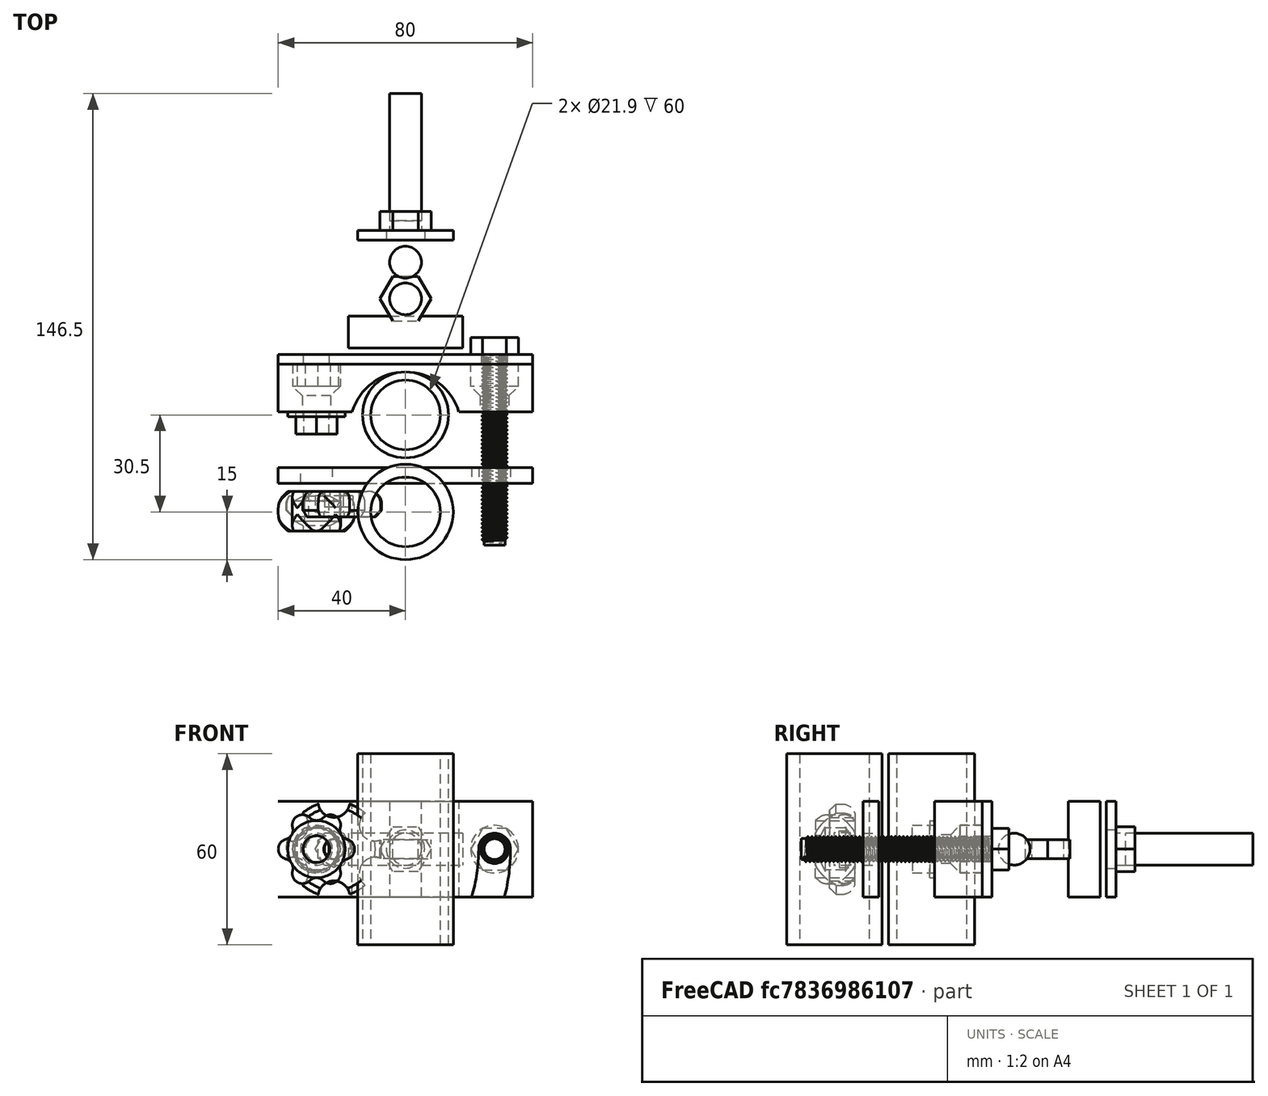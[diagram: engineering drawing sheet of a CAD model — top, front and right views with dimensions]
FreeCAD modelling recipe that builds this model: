
FCSTD DOCUMENT  (FreeCAD 1.0R39109 (Git))
Label: attache_remorque_V2
License: All rights reserved
LicenseURL: http://en.wikipedia.org/wiki/All_rights_reserved
objects: Sketcher::SketchObject×26, TechDraw::DrawViewBalloon×24, PartDesign::Body×16, PartDesign::Pad×15, TechDraw::DrawViewDimension×14, Part::FeaturePython×13, PartDesign::Pocket×6, TechDraw::DrawViewPart×4, PartDesign::Revolution×2, PartDesign::Groove×2, TechDraw::DrawSVGTemplate×1, PartDesign::AdditiveHelix×1, Spreadsheet::Sheet×1, TechDraw::DrawViewAnnotation×1, TechDraw::DrawPage×1
note: 159 computed .brp shape members not serialized (recipe doc carries the construction recipe); baked Part::Feature solids carry a one-line shape summary decoded from their .brp

FEATURE [Sketcher::SketchObject] Sketch
  ArcFitTolerance = 0
  AttachmentSupport = -> [XY_Plane]
  FullyConstrained = true
  MakeInternals = false
  MapMode = 5
  sketch-geometry (8):
    g0: LineSegment StartX=7 StartY=4.04145 StartZ=0 EndX=2.7e-15 EndY=8.0829 EndZ=0
    g1: LineSegment StartX=2.7e-15 StartY=8.0829 StartZ=0 EndX=-7 EndY=4.04145 EndZ=0
    g2: LineSegment StartX=-7 StartY=4.04145 StartZ=0 EndX=-7 EndY=-4.04145 EndZ=0
    g3: LineSegment StartX=-7 StartY=-4.04145 StartZ=0 EndX=4.17e-14 EndY=-8.0829 EndZ=0
    g4: LineSegment StartX=4.17e-14 StartY=-8.0829 StartZ=0 EndX=7 EndY=-4.04145 EndZ=0
    g5: LineSegment StartX=7 StartY=-4.04145 StartZ=0 EndX=7 EndY=4.04145 EndZ=0
    g6: Circle [constr] CenterX=0 CenterY=0 CenterZ=0 NormalX=0 NormalY=0 NormalZ=1 AngleXU=0 Radius=8.0829
    g7: Circle CenterX=0 CenterY=0 CenterZ=0 NormalX=0 NormalY=0 NormalZ=1 AngleXU=0 Radius=5
  constraints (18):
    c: Coincident(g0,g1)
    c: Coincident(g1,g2)
    c: Coincident(g2,g3)
    c: Coincident(g3,g4)
    c: Coincident(g4,g5)
    c: Coincident(g5,g0)
    c: Equal(g0, g1-g5) x5
    c: PointOnObject(g0,g6)
    c: PointOnObject(g1,g6)
    c: PointOnObject(g2,g6)
    c: PointOnObject(g3,g6)
    c: PointOnObject(g4,g6)
    c: PointOnObject(g5,g6)
    c: Coincident(g6,g-1)
    c: Vertical(g5)
    c: DistanceX(g2,g4) = 14
    c: Coincident(g7,g6)
    c: Radius(g7) = 5
FEATURE [PartDesign::Pad] Pad
  Direction = (0,0,1)
  Length = 6
  Length2 = 10
  Profile = -> Sketch
  ReferenceAxis = -> Sketch [N_Axis]
  Suppressed = false
  Type = 0
FEATURE [PartDesign::Body] Body  label="Ecrou M10"
  AllowCompound = false
  Group = -> [Sketch,Pad]
  Origin = -> Origin
  Placement = pos=(4e-16,2,-15) rot=(0,0,-1;0.523599rad)
  Tip = -> Pad
  expr: .Placement.Base.y = 2 + Spreadsheet.eclate * 80
  expr: .Placement.Base.z = -15 - Spreadsheet.eclate * 10
FEATURE [Sketcher::SketchObject] Sketch001
  ArcFitTolerance = 0
  AttachmentSupport = -> [XY_Plane001]
  FullyConstrained = true
  MakeInternals = false
  MapMode = 5
  sketch-geometry (1):
    g0: Circle CenterX=0 CenterY=0 CenterZ=0 NormalX=0 NormalY=0 NormalZ=1 AngleXU=0 Radius=5
  constraints (2):
    c: Coincident(g0,g-1)
    c: Radius(g0) = 5
FEATURE [PartDesign::Pad] Pad001
  Direction = (0,0,1)
  Length = 30
  Length2 = 10
  Midplane = true
  Profile = -> Sketch001
  ReferenceAxis = -> Sketch001 [N_Axis]
  Suppressed = false
  Type = 0
FEATURE [PartDesign::Body] Body001  label="Tige Filetée M10x30"
  AllowCompound = false
  Group = -> [Sketch001,Pad001]
  Origin = -> Origin001
  Placement = pos=(0,2,0) rot=(0,0,1;0rad)
  Tip = -> Pad001
  expr: .Placement.Base.y = 2 + Spreadsheet.eclate * 80
FEATURE [Part::FeaturePython] Clone  label="Ecrou M011"  # Draft clone (typed FeaturePython)
  AttacherType = Attacher::AttachEngine3D
  Fuse = false
  Objects = -> [Body]
  Placement = pos=(1.3e-15,2,9) rot=(0,0,-1;0.523599rad)
  Scale = (1,1,1)
  expr: .Placement.Base.y = 2 + Spreadsheet.eclate * 80
  expr: .Placement.Base.z = 9 + Spreadsheet.eclate * 10
FEATURE [Sketcher::SketchObject] Sketch002
  ArcFitTolerance = 0
  AttachmentSupport = -> [XY_Plane002]
  FullyConstrained = true
  MakeInternals = false
  MapMode = 5
  sketch-geometry (1):
    g0: Circle CenterX=0 CenterY=0 CenterZ=0 NormalX=0 NormalY=0 NormalZ=1 AngleXU=0 Radius=5
  constraints (2):
    c: Coincident(g0,g-1)
    c: Radius(g0) = 5
FEATURE [PartDesign::Pad] Pad002
  Direction = (0,0,1)
  Length = 36
  Length2 = 10
  Midplane = true
  Profile = -> Sketch002
  ReferenceAxis = -> Sketch002 [N_Axis]
  Suppressed = false
  Type = 0
FEATURE [PartDesign::Body] Body002  label="Tige Filetée M10 x 36"
  AllowCompound = false
  Group = -> [Sketch002,Pad002]
  Origin = -> Origin002
  Placement = pos=(0,-20,0) rot=(0,-1,0;1.5708rad)
  Tip = -> Pad002
  expr: .Placement.Base.y = -20 + Spreadsheet.eclate * 60
FEATURE [Part::FeaturePython] Clone001  label="Ecrou M012"  # Draft clone (typed FeaturePython)
  AttacherType = Attacher::AttachEngine3D
  Fuse = false
  Objects = -> [Clone]
  Placement = pos=(12,-20,0) rot=(-0.248932,0.935984,-0.248932;1.63782rad)
  Scale = (1,1,1)
  expr: .Placement.Base.x = 12 + Spreadsheet.eclate * 10
  expr: .Placement.Base.y = -20 + Spreadsheet.eclate * 60
FEATURE [Part::FeaturePython] Clone002  label="Ecrou M013"  # Draft clone (typed FeaturePython)
  AttacherType = Attacher::AttachEngine3D
  Fuse = false
  Objects = -> [Clone001]
  Placement = pos=(-18,-20,0) rot=(0.57735,0.57735,0.57735;2.0944rad)
  Scale = (1,1,1)
  expr: .Placement.Base.x = -18 - Spreadsheet.eclate * 10
  expr: .Placement.Base.y = -20 + Spreadsheet.eclate * 60
FEATURE [Sketcher::SketchObject] Sketch003
  ArcFitTolerance = 0
  AttachmentSupport = -> [YZ_Plane003]
  FullyConstrained = true
  MakeInternals = false
  MapMode = 5
  Placement = pos=(0,0,0) rot=(0.57735,0.57735,0.57735;2.0944rad)
  sketch-geometry (4):
    g0: LineSegment StartX=0 StartY=15 StartZ=0 EndX=3 EndY=15 EndZ=0
    g1: LineSegment StartX=3 StartY=15 StartZ=0 EndX=3 EndY=-15 EndZ=0
    g2: LineSegment StartX=3 StartY=-15 StartZ=0 EndX=0 EndY=-15 EndZ=0
    g3: LineSegment StartX=0 StartY=-15 StartZ=0 EndX=0 EndY=15 EndZ=0
  constraints (11):
    c: Coincident(g0,g1)
    c: Coincident(g1,g2)
    c: Coincident(g2,g3)
    c: Coincident(g3,g0)
    c: Horizontal(g0)
    c: Horizontal(g2)
    c: Vertical(g3)
    c: PointOnObject(g0,g-2)
    c: DistanceX(g2,g2) = 3
    c: Symmetric(g1,g0,g-1)
    c: DistanceY(g1,g1) = 30
FEATURE [PartDesign::Pad] Pad003
  Direction = (1,0,0)
  Length = 30
  Length2 = 10
  Midplane = true
  Placement = pos=(0,0,0) rot=(0.57735,0.57735,0.57735;2.0944rad)
  Profile = -> Sketch003
  ReferenceAxis = -> Sketch003 [N_Axis]
  Suppressed = false
  Type = 0
FEATURE [Part::FeaturePython] Clone003  label="Ecrou M014"  # Draft clone (typed FeaturePython)
  AttacherType = Attacher::AttachEngine3D
  Fuse = false
  Objects = -> [Clone002]
  Placement = pos=(0,12,0) rot=(-0.57735,0.57735,0.57735;2.0944rad)
  Scale = (1,1,1)
  expr: .Placement.Base.y = 12 + Spreadsheet.eclate * 100
FEATURE [Sketcher::SketchObject] Sketch004
  ArcFitTolerance = 0
  AttachmentSupport = -> [XY_Plane004]
  FullyConstrained = true
  MakeInternals = false
  MapMode = 5
  sketch-geometry (1):
    g0: Circle CenterX=0 CenterY=0 CenterZ=0 NormalX=0 NormalY=0 NormalZ=1 AngleXU=0 Radius=5
  constraints (2):
    c: Coincident(g0,g-1)
    c: Radius(g0) = 5
FEATURE [PartDesign::Pad] Pad004
  Direction = (0,0,1)
  Length = 40
  Length2 = 10
  Midplane = true
  Profile = -> Sketch004
  ReferenceAxis = -> Sketch004 [N_Axis]
  Suppressed = false
  Type = 0
FEATURE [PartDesign::Body] Body004  label="Tige Filetée M10 002"
  AllowCompound = false
  Group = -> [Sketch004,Pad004]
  Origin = -> Origin004
  Placement = pos=(0,35,0) rot=(0.57735,-0.57735,-0.57735;4.18879rad)
  Tip = -> Pad004
  expr: .Placement.Base.y = 35 + Spreadsheet.eclate * 110
FEATURE [Sketcher::SketchObject] Sketch005
  ArcFitTolerance = 0
  AttachmentSupport = -> [XY_Plane005]
  FullyConstrained = false
  MakeInternals = false
  MapMode = 5
  sketch-geometry (2):
    g0: Circle CenterX=0 CenterY=-13.5 CenterZ=0 NormalX=0 NormalY=0 NormalZ=1 AngleXU=0 Radius=13.5
    g1: Circle CenterX=0 CenterY=-13.5 CenterZ=0 NormalX=0 NormalY=0 NormalZ=1 AngleXU=0 Radius=10.9492
  constraints (4):
    c: Radius(g0) = 13.5
    c: Coincident(g1,g0)
    c: PointOnObject(g0,g-2)
    c: Tangent(g0,g-1)
FEATURE [PartDesign::Pad] Pad005
  Direction = (0,0,1)
  Length = 60
  Length2 = 10
  Midplane = true
  Profile = -> Sketch005
  ReferenceAxis = -> Sketch005 [N_Axis]
  Suppressed = false
  Type = 0
FEATURE [PartDesign::Body] Body005  label="Tige de selle 27mm"
  AllowCompound = false
  Group = -> [Sketch005,Pad005]
  Origin = -> Origin005
  Placement = pos=(0,-32.5,0) rot=(0,0,1;0rad)
  Tip = -> Pad005
FEATURE [Part::FeaturePython] Clone004  label="Ecrou M015"  # Draft clone (typed FeaturePython)
  AttacherType = Attacher::AttachEngine3D
  Fuse = false
  Objects = -> [Body]
  Placement = pos=(0,-9.5,-3) rot=(0,0,-1;5.75959rad)
  Scale = (1,1,1)
  expr: .Placement.Base.y = -9.5 + Spreadsheet.eclate * 70
FEATURE [Sketcher::SketchObject] Sketch007
  ArcFitTolerance = 0
  AttachmentSupport = -> [XY_Plane007]
  FullyConstrained = true
  MakeInternals = false
  MapMode = 5
  sketch-geometry (6):
    g0: LineSegment StartX=-16.7705 StartY=-15 StartZ=0 EndX=-40 EndY=-15 EndZ=0
    g1: LineSegment StartX=-40 StartY=-15 StartZ=0 EndX=-40 EndY=0 EndZ=0
    g2: LineSegment StartX=-40 StartY=0 StartZ=0 EndX=40 EndY=0 EndZ=0
    g3: LineSegment StartX=40 StartY=0 StartZ=0 EndX=40 EndY=-15 EndZ=0
    g4: LineSegment StartX=40 StartY=-15 StartZ=0 EndX=16.7705 EndY=-15 EndZ=0
    g5: ArcOfCircle CenterX=5e-16 CenterY=-20 CenterZ=0 NormalX=0 NormalY=0 NormalZ=1 AngleXU=0 Radius=17.5 StartAngle=0.289752 EndAngle=2.85184
  constraints (17):
    c: Horizontal(g0)
    c: Coincident(g0,g1)
    c: PointOnObject(g1,g-1)
    c: Vertical(g1)
    c: Coincident(g1,g2)
    c: PointOnObject(g2,g-1)
    c: Coincident(g2,g3)
    c: Vertical(g3)
    c: Coincident(g3,g4)
    c: Coincident(g5,g0)
    c: Coincident(g5,g4)
    c: Radius(g5) = 17.5
    c: Symmetric(g0,g4,g-2)
    c: Symmetric(g3,g0,g-2)
    c: DistanceX(g2,g2) = 80
    c: DistanceY(g3,g3) = 15
    c: DistanceY(g5) = -20
FEATURE [PartDesign::Pad] Pad007
  Direction = (0,0,1)
  Length = 30
  Length2 = 10
  Midplane = true
  Profile = -> Sketch007
  ReferenceAxis = -> Sketch007 [N_Axis]
  Suppressed = false
  Type = 0
FEATURE [Sketcher::SketchObject] Sketch010
  ArcFitTolerance = 0
  AttachmentSupport = -> [XY_Plane008]
  FullyConstrained = true
  MakeInternals = false
  MapMode = 5
  sketch-geometry (5):
    g0: LineSegment StartX=0 StartY=0 StartZ=0 EndX=-40 EndY=0 EndZ=0
    g1: LineSegment StartX=-40 StartY=0 StartZ=0 EndX=-40 EndY=-5 EndZ=0
    g2: LineSegment StartX=-40 StartY=-5 StartZ=0 EndX=40 EndY=-5 EndZ=0
    g3: LineSegment StartX=40 StartY=-5 StartZ=0 EndX=40 EndY=0 EndZ=0
    g4: LineSegment StartX=40 StartY=0 StartZ=0 EndX=0 EndY=0 EndZ=0
  constraints (14):
    c: PointOnObject(g0,g-1)
    c: PointOnObject(g0,g-1)
    c: Coincident(g0,g1)
    c: Vertical(g1)
    c: Coincident(g1,g2)
    c: Coincident(g2,g3)
    c: Vertical(g3)
    c: Coincident(g3,g4)
    c: Horizontal(g4)
    c: Symmetric(g2,g1,g-2)
    c: DistanceY(g3,g3) = 5
    c: DistanceX(g2,g2) = 80
    c: Coincident(g4,g0)
    c: PointOnObject(g0,g-2)
FEATURE [PartDesign::Pad] Pad009
  Direction = (0,0,1)
  Length = 30
  Length2 = 10
  Midplane = true
  Profile = -> Sketch010
  ReferenceAxis = -> Sketch010 [N_Axis]
  Suppressed = false
  Type = 0
FEATURE [Sketcher::SketchObject] Sketch011
  ArcFitTolerance = 0
  AttachmentSupport = -> [XZ_Plane008]
  FullyConstrained = true
  MakeInternals = false
  MapMode = 5
  Placement = pos=(0,0,0) rot=(1,0,0;1.5708rad)
  sketch-geometry (5):
    g0: ArcOfCircle CenterX=-28 CenterY=0 CenterZ=0 NormalX=0 NormalY=0 NormalZ=1 AngleXU=0 Radius=51 StartAngle=5.98465 EndAngle=6.28319
    g1: ArcOfCircle CenterX=-28 CenterY=0 CenterZ=0 NormalX=0 NormalY=0 NormalZ=1 AngleXU=0 Radius=61 StartAngle=6.03474 EndAngle=6.28319
    g2: LineSegment StartX=20.7442 StartY=-15 StartZ=0 EndX=31.127 EndY=-15 EndZ=0
    g3: ArcOfCircle CenterX=28 CenterY=0 CenterZ=0 NormalX=0 NormalY=0 NormalZ=1 AngleXU=0 Radius=5 StartAngle=0 EndAngle=3.14159
    g4: Circle CenterX=-28 CenterY=0 CenterZ=0 NormalX=0 NormalY=0 NormalZ=1 AngleXU=0 Radius=5
  constraints (13):
    c: Coincident(g1,g0)
    c: Coincident(g2,g0)
    c: Coincident(g2,g1)
    c: PointOnObject(g3,g-1)
    c: Radius(g3) = 5
    c: DistanceX(g3) = 28
    c: Horizontal(g2)
    c: Tangent(g3,g0) = 1.5708
    c: Tangent(g3,g1) = -1.5708
    c: DistanceY(g1) = -15
    c: Equal(g4,g3)
    c: Symmetric(g3,g4,g-2)
    c: Coincident(g0,g4)
FEATURE [PartDesign::Pocket] Pocket001
  BaseFeature = -> Pad009
  Direction = (0,1,-2e-16)
  Length = 5
  Length2 = 5
  Profile = -> Sketch011
  ReferenceAxis = -> Sketch011 [N_Axis]
  Reversed = true
  Suppressed = false
  Type = 0
FEATURE [PartDesign::Body] Body008  label="Contre plaque selle"
  AllowCompound = false
  Group = -> [Sketch010,Pad009,Sketch011,Pocket001]
  Origin = -> Origin008
  Placement = pos=(0,-62.5,0) rot=(0,0,1;0rad)
  Tip = -> Pocket001
  expr: .Placement.Base.y = -62.5 - Spreadsheet.eclate * 10
FEATURE [Sketcher::SketchObject] Sketch012
  ArcFitTolerance = 0
  AttachmentSupport = -> [XY_Plane009]
  FullyConstrained = true
  MakeInternals = false
  MapMode = 5
  sketch-geometry (8):
    g0: LineSegment StartX=5 StartY=2.88675 StartZ=0 EndX=9.4058e-12 EndY=5.7735 EndZ=0
    g1: LineSegment StartX=9.4058e-12 StartY=5.7735 StartZ=0 EndX=-5 EndY=2.88675 EndZ=0
    g2: LineSegment StartX=-5 StartY=2.88675 StartZ=0 EndX=-5 EndY=-2.88675 EndZ=0
    g3: LineSegment StartX=-5 StartY=-2.88675 StartZ=0 EndX=-1.4424e-12 EndY=-5.7735 EndZ=0
    g4: LineSegment StartX=-1.4424e-12 StartY=-5.7735 StartZ=0 EndX=5 EndY=-2.88675 EndZ=0
    g5: LineSegment StartX=5 StartY=-2.88675 StartZ=0 EndX=5 EndY=2.88675 EndZ=0
    g6: Circle [constr] CenterX=0 CenterY=0 CenterZ=0 NormalX=0 NormalY=0 NormalZ=1 AngleXU=0 Radius=5.7735
    g7: Circle CenterX=0 CenterY=0 CenterZ=0 NormalX=0 NormalY=0 NormalZ=1 AngleXU=0 Radius=3
  constraints (18):
    c: Coincident(g0,g1)
    c: Coincident(g1,g2)
    c: Coincident(g2,g3)
    c: Coincident(g3,g4)
    c: Coincident(g4,g5)
    c: Coincident(g5,g0)
    c: Equal(g0, g1-g5) x5
    c: PointOnObject(g0,g6)
    c: PointOnObject(g1,g6)
    c: PointOnObject(g2,g6)
    c: PointOnObject(g3,g6)
    c: PointOnObject(g4,g6)
    c: PointOnObject(g5,g6)
    c: Coincident(g6,g-1)
    c: Vertical(g5)
    c: DistanceX(g2,g4) = 10
    c: Coincident(g7,g6)
    c: Radius(g7) = 3
FEATURE [PartDesign::Pad] Pad010
  Direction = (0,0,1)
  Length = 5
  Length2 = 10
  Profile = -> Sketch012
  ReferenceAxis = -> Sketch012 [N_Axis]
  Suppressed = false
  Type = 0
FEATURE [PartDesign::Body] Body009  label="Ecrou M6 001"
  AllowCompound = false
  Group = -> [Sketch012,Pad010]
  Origin = -> Origin009
  Placement = pos=(22.5,-75,-4e-15) rot=(1,0,0;4.71239rad)
  Tip = -> Pad010
FEATURE [Part::FeaturePython] Clone005  label="Ecrou M6 002"  # Draft clone (typed FeaturePython)
  AttacherType = Attacher::AttachEngine3D
  Fuse = false
  Objects = -> [Body009]
  Placement = pos=(-22.5,-75,-4e-15) rot=(1,0,0;4.71239rad)
  Scale = (1,1,1)
FEATURE [Sketcher::SketchObject] Sketch013
  ArcFitTolerance = 0
  AttachmentSupport = -> [XY_Plane010]
  FullyConstrained = false
  MakeInternals = false
  MapMode = 5
  sketch-geometry (2):
    g0: Circle CenterX=0 CenterY=-15 CenterZ=0 NormalX=0 NormalY=0 NormalZ=1 AngleXU=0 Radius=15
    g1: Circle CenterX=0 CenterY=-15 CenterZ=0 NormalX=0 NormalY=0 NormalZ=1 AngleXU=0 Radius=10.9492
  constraints (4):
    c: Radius(g0) = 15
    c: Coincident(g1,g0)
    c: PointOnObject(g0,g-2)
    c: Tangent(g0,g-1)
FEATURE [PartDesign::Pad] Pad011
  Direction = (0,0,1)
  Length = 60
  Length2 = 10
  Midplane = true
  Profile = -> Sketch013
  ReferenceAxis = -> Sketch013 [N_Axis]
  Suppressed = false
  Type = 0
FEATURE [PartDesign::Body] Body010  label="Tige de selle 30mm"
  AllowCompound = false
  Group = -> [Sketch013,Pad011]
  Origin = -> Origin010
  Placement = pos=(0,-61.5,0) rot=(0,0,1;0rad)
  Tip = -> Pad011
FEATURE [Sketcher::SketchObject] Sketch014
  ArcFitTolerance = 0
  AttachmentSupport = -> [XZ_Plane011]
  FullyConstrained = true
  MakeInternals = false
  MapMode = 5
  Placement = pos=(0,0,0) rot=(1,0,0;1.5708rad)
  sketch-geometry (6):
    g0: ArcOfCircle CenterX=11 CenterY=-4 CenterZ=0 NormalX=0 NormalY=0 NormalZ=1 AngleXU=0 Radius=4 StartAngle=0 EndAngle=1.5708
    g1: LineSegment StartX=3.2 StartY=0 StartZ=0 EndX=3.2 EndY=-8 EndZ=0
    g2: LineSegment StartX=3.2 StartY=-8 StartZ=0 EndX=13 EndY=-8 EndZ=0
    g3: LineSegment StartX=15 StartY=-6 StartZ=0 EndX=15 EndY=-4 EndZ=0
    g4: LineSegment StartX=13 StartY=-8 StartZ=0 EndX=15 EndY=-6 EndZ=0
    g5: LineSegment StartX=3.2 StartY=0 StartZ=0 EndX=11 EndY=0 EndZ=0
  constraints (17):
    c: Vertical(g1)
    c: Coincident(g1,g2)
    c: Horizontal(g2)
    c: Vertical(g3)
    c: Tangent(g3,g0) = -1.5708
    c: DistanceX(g1) = 3.2
    c: DistanceX(g3) = 15
    c: DistanceY(g3,g3) = 2
    c: Coincident(g4,g2)
    c: Coincident(g4,g3)
    c: DistanceX(g4,g4) = 2
    c: DistanceY(g4,g4) = 2
    c: Coincident(g1,g5)
    c: PointOnObject(g1,g-1)
    c: Horizontal(g5)
    c: Tangent(g5,g0) = 1.5708
    c: DistanceY(g2,g0) = 8
FEATURE [Sketcher::SketchObject] Sketch015
  ArcFitTolerance = 0
  AttachmentOffset = pos=(0,0,-1.5) rot=(0,0,1;0rad)
  AttachmentSupport = -> [XY_Plane011]
  FullyConstrained = true
  MakeInternals = false
  MapMode = 5
  Placement = pos=(0,0,-1.5) rot=(0,0,1;0rad)
  sketch-geometry (7):
    g0: LineSegment StartX=5.88897 StartY=0 StartZ=0 EndX=2.94449 EndY=5.1 EndZ=0
    g1: LineSegment StartX=2.94449 StartY=5.1 StartZ=0 EndX=-2.94449 EndY=5.1 EndZ=0
    g2: LineSegment StartX=-2.94449 StartY=5.1 StartZ=0 EndX=-5.88897 EndY=0 EndZ=0
    g3: LineSegment StartX=-5.88897 StartY=0 StartZ=0 EndX=-2.94449 EndY=-5.1 EndZ=0
    g4: LineSegment StartX=-2.94449 StartY=-5.1 StartZ=0 EndX=2.94449 EndY=-5.1 EndZ=0
    g5: LineSegment StartX=2.94449 StartY=-5.1 StartZ=0 EndX=5.88897 EndY=0 EndZ=0
    g6: Circle [constr] CenterX=0 CenterY=0 CenterZ=0 NormalX=0 NormalY=0 NormalZ=1 AngleXU=0 Radius=5.88897
  constraints (16):
    c: Coincident(g0,g1)
    c: Coincident(g1,g2)
    c: Coincident(g2,g3)
    c: Coincident(g3,g4)
    c: Coincident(g4,g5)
    c: Coincident(g5,g0)
    c: Equal(g0, g1-g5) x5
    c: PointOnObject(g0,g6)
    c: PointOnObject(g1,g6)
    c: PointOnObject(g2,g6)
    c: PointOnObject(g3,g6)
    c: PointOnObject(g4,g6)
    c: PointOnObject(g5,g6)
    c: Coincident(g6,g-1)
    c: PointOnObject(g5,g-1)
    c: DistanceY(g4,g0) = 10.2
FEATURE [Sketcher::SketchObject] Sketch016
  ArcFitTolerance = 0
  AttachmentSupport = -> [XY_Plane011]
  FullyConstrained = true
  MakeInternals = false
  MapMode = 5
  sketch-geometry (13):
    g0: Circle CenterX=0 CenterY=15 CenterZ=0 NormalX=0 NormalY=0 NormalZ=1 AngleXU=0 Radius=5
    g1: Circle CenterX=12.9904 CenterY=7.5 CenterZ=0 NormalX=0 NormalY=0 NormalZ=1 AngleXU=0 Radius=5
    g2: Circle CenterX=12.9904 CenterY=-7.5 CenterZ=0 NormalX=0 NormalY=0 NormalZ=1 AngleXU=0 Radius=5
    g3: Circle CenterX=0 CenterY=-15 CenterZ=0 NormalX=0 NormalY=0 NormalZ=1 AngleXU=0 Radius=5
    g4: Circle CenterX=-12.9904 CenterY=-7.5 CenterZ=0 NormalX=0 NormalY=0 NormalZ=1 AngleXU=0 Radius=5
    g5: Circle CenterX=-12.9904 CenterY=7.5 CenterZ=0 NormalX=0 NormalY=0 NormalZ=1 AngleXU=0 Radius=5
    g6: LineSegment [constr] StartX=0 StartY=15 StartZ=0 EndX=-12.9904 EndY=7.5 EndZ=0
    g7: LineSegment [constr] StartX=-12.9904 StartY=7.5 StartZ=0 EndX=-12.9904 EndY=-7.5 EndZ=0
    g8: LineSegment [constr] StartX=-12.9904 StartY=-7.5 StartZ=0 EndX=0 EndY=-15 EndZ=0
    g9: LineSegment [constr] StartX=0 StartY=-15 StartZ=0 EndX=12.9904 EndY=-7.5 EndZ=0
    g10: LineSegment [constr] StartX=12.9904 StartY=-7.5 StartZ=0 EndX=12.9904 EndY=7.5 EndZ=0
    g11: LineSegment [constr] StartX=12.9904 StartY=7.5 StartZ=0 EndX=0 EndY=15 EndZ=0
    g12: Circle [constr] CenterX=0 CenterY=0 CenterZ=0 NormalX=0 NormalY=0 NormalZ=1 AngleXU=0 Radius=15
  constraints (28):
    c: PointOnObject(g0,g-2)
    c: PointOnObject(g3,g-2)
    c: Coincident(g6,g7)
    c: Coincident(g7,g8)
    c: Coincident(g8,g9)
    c: Coincident(g9,g10)
    c: Coincident(g10,g11)
    c: Coincident(g11,g6)
    c: Equal(g6, g7-g11) x5
    c: PointOnObject(g6,g12)
    c: PointOnObject(g7,g12)
    c: PointOnObject(g8,g12)
    c: PointOnObject(g9,g12)
    c: PointOnObject(g11,g12)
    c: Coincident(g12,g-1)
    c: Coincident(g11,g0)
    c: Coincident(g10,g1)
    c: Coincident(g2,g9)
    c: Coincident(g3,g8)
    c: Coincident(g4,g7)
    c: Coincident(g5,g6)
    c: Equal(g4,g5)
    c: Equal(g5,g0)
    c: Equal(g0,g1)
    c: Equal(g1,g2)
    c: Equal(g2,g3)
    c: Radius(g1) = 5
    c: Radius(g12) = 15
FEATURE [PartDesign::Revolution] Revolution
  Angle = 360
  Angle2 = 60
  Axis = (0,2e-16,1)
  Base = (0,0,0)
  Placement = pos=(0,0,0) rot=(1,0,0;1.5708rad)
  Profile = -> Sketch014
  ReferenceAxis = -> Sketch014 [V_Axis]
  Reversed = true
  Suppressed = false
  Type = 0
FEATURE [PartDesign::Pocket] Pocket002
  BaseFeature = -> Revolution
  Direction = (0,0,-1)
  Length = 5
  Length2 = 5
  Placement = pos=(0,0,0) rot=(1,0,0;1.5708rad)
  Profile = -> Sketch016
  ReferenceAxis = -> Sketch016 [N_Axis]
  Suppressed = false
  Type = 1
FEATURE [PartDesign::Pocket] Pocket003
  BaseFeature = -> Pocket002
  Direction = (0,0,-1)
  Length = 5.2
  Length2 = 5
  Placement = pos=(0,0,0) rot=(1,0,0;1.5708rad)
  Profile = -> Sketch015
  ReferenceAxis = -> Sketch015 [N_Axis]
  Suppressed = false
  Type = 0
FEATURE [PartDesign::Body] Body011  label="Exterieur Boulon M6 001"
  AllowCompound = false
  Group = -> [Sketch014,Sketch015,Sketch016,Revolution,Pocket002,Pocket003]
  Origin = -> Origin011
  Placement = pos=(22.5,-70,1.55e-14) rot=(1,0,0;4.71239rad)
  Tip = -> Pocket003
FEATURE [Part::FeaturePython] Clone006  label="Exterieur Boulon M6 002"  # Draft clone (typed FeaturePython)
  AttacherType = Attacher::AttachEngine3D
  Fuse = false
  Objects = -> [Body011]
  Placement = pos=(-22.5,-70,1.55e-14) rot=(1,0,0;4.71239rad)
  Scale = (1,1,1)
FEATURE [Sketcher::SketchObject] Sketch017
  ArcFitTolerance = 0
  AttachmentOffset = pos=(28,0,0) rot=(0,0,1;0rad)
  AttachmentSupport = -> [XY_Plane007]
  FullyConstrained = true
  MakeInternals = false
  MapMode = 5
  Placement = pos=(28,0,0) rot=(0,0,1;0rad)
  sketch-geometry (6):
    g0: LineSegment StartX=0 StartY=0 StartZ=0 EndX=7.5 EndY=0 EndZ=0
    g1: LineSegment StartX=4.5 StartY=-10 StartZ=0 EndX=4.5 EndY=-27 EndZ=0
    g2: LineSegment StartX=4.5 StartY=-27 StartZ=0 EndX=0 EndY=-27 EndZ=0
    g3: LineSegment StartX=0 StartY=-27 StartZ=0 EndX=0 EndY=0 EndZ=0
    g4: LineSegment StartX=7.5 StartY=-7 StartZ=0 EndX=7.5 EndY=0 EndZ=0
    g5: LineSegment StartX=4.5 StartY=-10 StartZ=0 EndX=7.5 EndY=-7 EndZ=0
  constraints (17):
    c: Coincident(g-1,g0)
    c: PointOnObject(g0,g-1)
    c: Vertical(g1)
    c: Coincident(g1,g2)
    c: PointOnObject(g2,g-2)
    c: Horizontal(g2)
    c: Coincident(g2,g3)
    c: Coincident(g3,g0)
    c: DistanceX(g2,g2) = 4.5
    c: Coincident(g4,g0)
    c: Vertical(g4)
    c: DistanceX(g4) = 7.5
    c: DistanceY(g4,g4) = 7
    c: DistanceY(g1,g4) = 20
    c: Coincident(g5,g1)
    c: Coincident(g5,g4)
    c: Angle(g5) = 0.785398
FEATURE [Sketcher::SketchObject] Sketch018
  ArcFitTolerance = 0
  AttachmentOffset = pos=(-28,0,0) rot=(0,0,1;0rad)
  AttachmentSupport = -> [XY_Plane007]
  FullyConstrained = true
  MakeInternals = false
  MapMode = 5
  Placement = pos=(-28,0,0) rot=(0,0,1;0rad)
  sketch-geometry (6):
    g0: LineSegment StartX=0 StartY=0 StartZ=0 EndX=7.5 EndY=0 EndZ=0
    g1: LineSegment StartX=4.5 StartY=-10 StartZ=0 EndX=4.5 EndY=-30 EndZ=0
    g2: LineSegment StartX=4.5 StartY=-30 StartZ=0 EndX=0 EndY=-30 EndZ=0
    g3: LineSegment StartX=0 StartY=-30 StartZ=0 EndX=0 EndY=0 EndZ=0
    g4: LineSegment StartX=7.5 StartY=0 StartZ=0 EndX=7.5 EndY=-7 EndZ=0
    g5: LineSegment StartX=7.5 StartY=-7 StartZ=0 EndX=4.5 EndY=-10 EndZ=0
  constraints (17):
    c: Coincident(g-1,g0)
    c: PointOnObject(g0,g-1)
    c: Vertical(g1)
    c: Coincident(g1,g2)
    c: PointOnObject(g2,g-2)
    c: Horizontal(g2)
    c: Coincident(g2,g3)
    c: Coincident(g3,g0)
    c: DistanceX(g2,g2) = 4.5
    c: DistanceY(g1,g1) = 20
    c: Coincident(g0,g4)
    c: Vertical(g4)
    c: DistanceX(g4) = 7.5
    c: DistanceY(g4,g4) = 7
    c: Coincident(g5,g4)
    c: Coincident(g5,g1)
    c: Angle(g5) = -2.35619
FEATURE [PartDesign::Groove] Groove
  Angle = 360
  Angle2 = 60
  Axis = (0,1,0)
  Base = (28,0,0)
  BaseFeature = -> Pad007
  Profile = -> Sketch017
  ReferenceAxis = -> Sketch017 [V_Axis]
  Suppressed = false
  Type = 0
FEATURE [PartDesign::Groove] Groove001
  Angle = 360
  Angle2 = 60
  Axis = (0,1,0)
  Base = (-28,0,0)
  BaseFeature = -> Groove
  Profile = -> Sketch018
  ReferenceAxis = -> Sketch018 [V_Axis]
  Suppressed = false
  Type = 0
FEATURE [PartDesign::Body] Body007  label="DemiTube Maitnient selle"
  AllowCompound = false
  Group = -> [Sketch007,Pad007,Sketch017,Sketch018,Groove,Groove001]
  Origin = -> Origin007
  Placement = pos=(0,-30,0) rot=(0,0,1;0rad)
  Tip = -> Groove001
  expr: .Placement.Base.y = -30 + Spreadsheet.eclate * 20
FEATURE [Sketcher::SketchObject] Sketch019
  ArcFitTolerance = 0
  AttachmentSupport = -> [XZ_Plane012]
  FullyConstrained = true
  MakeInternals = false
  MapMode = 5
  Placement = pos=(0,0,0) rot=(1,0,0;1.5708rad)
  expr: Constraints[8] = 6.5 + 6
  sketch-geometry (14):
    g0: LineSegment StartX=4.2 StartY=-12.5 StartZ=0 EndX=9 EndY=-12.5 EndZ=0
    g1: LineSegment StartX=12 StartY=-7.24264 StartZ=0 EndX=12 EndY=-5.25736 EndZ=0
    g2: LineSegment StartX=4.2 StartY=0 StartZ=0 EndX=9 EndY=0 EndZ=0
    g3: LineSegment StartX=4.2 StartY=0 StartZ=0 EndX=4.2 EndY=-1.6 EndZ=0
    g4: LineSegment StartX=6.6 StartY=-3.1 StartZ=0 EndX=6.6 EndY=-9.4 EndZ=0
    g5: LineSegment StartX=4.2 StartY=-10.9 StartZ=0 EndX=4.2 EndY=-12.5 EndZ=0
    g6: LineSegment StartX=6.6 StartY=-9.4 StartZ=0 EndX=7 EndY=-9.4 EndZ=0
    g7: LineSegment StartX=7 StartY=-9.4 StartZ=0 EndX=4.2 EndY=-10.9 EndZ=0
    g8: LineSegment StartX=6.6 StartY=-3.1 StartZ=0 EndX=7 EndY=-3.1 EndZ=0
    g9: LineSegment StartX=7 StartY=-3.1 StartZ=0 EndX=4.2 EndY=-1.6 EndZ=0
    g10: ArcOfCircle CenterX=6.55025 CenterY=-5.25736 CenterZ=0 NormalX=0 NormalY=0 NormalZ=1 AngleXU=0 Radius=5.44975 StartAngle=0 EndAngle=0.785398
    g11: ArcOfCircle CenterX=6.55025 CenterY=-7.24264 CenterZ=0 NormalX=0 NormalY=0 NormalZ=1 AngleXU=0 Radius=5.44975 StartAngle=5.49779 EndAngle=6.28319
    g12: LineSegment StartX=9 StartY=0 StartZ=0 EndX=10.4038 EndY=-1.40381 EndZ=0
    g13: LineSegment StartX=9 StartY=-12.5 StartZ=0 EndX=10.4038 EndY=-11.0962 EndZ=0
  constraints (42):
    c: Horizontal(g0)
    c: Vertical(g1)
    c: DistanceX(g2) = 4.2
    c: DistanceX(g1) = 12
    c: DistanceX(g0,g1) = 3
    c: PointOnObject(g2,g-1)
    c: Horizontal(g2)
    c: Vertical(g0,g2)
    c: DistanceY(g0,g2) = 12.5
    c: Coincident(g2,g3)
    c: Vertical(g3)
    c: Vertical(g4)
    c: Coincident(g5,g0)
    c: Vertical(g5)
    c: Vertical(g5,g3)
    c: Equal(g5,g3)
    c: DistanceX(g-1,g4) = 6.6
    c: Coincident(g4,g6)
    c: Horizontal(g6)
    c: Coincident(g6,g7)
    c: Coincident(g7,g5)
    c: Coincident(g4,g8)
    c: Horizontal(g8)
    c: Coincident(g8,g9)
    c: Coincident(g9,g3)
    c: Vertical(g8,g6)
    c: DistanceX(g-1,g6) = 7
    c: Equal(g7,g9)
    c: DistanceY(g4,g4) = 6.3
    c: DistanceY(g9,g9) = 1.5
    c: Coincident(g10,g1)
    c: Coincident(g11,g1)
    c: Coincident(g12,g2)
    c: Coincident(g13,g0)
    c: Tangent(g12,g10) = 1.5708
    c: Tangent(g13,g11) = -1.5708
    c: Angle(g12) = -0.785398
    c: Equal(g11,g10)
    c: Equal(g13,g12)
    c: Horizontal(g1,g10)
    c: Horizontal(g1,g11)
    c: Equal(g12,g1)
FEATURE [PartDesign::Revolution] Revolution001
  Angle = 360
  Angle2 = 60
  Axis = (0,2e-16,1)
  Base = (0,0,0)
  Placement = pos=(0,0,0) rot=(1,0,0;1.5708rad)
  Profile = -> Sketch019
  ReferenceAxis = -> Sketch019 [V_Axis]
  Reversed = true
  Suppressed = false
  Type = 0
FEATURE [Sketcher::SketchObject] Sketch020
  ArcFitTolerance = 0
  AttachmentOffset = pos=(0,0,-3) rot=(0,0,1;0rad)
  AttachmentSupport = -> [XY_Plane012]
  FullyConstrained = true
  MakeInternals = false
  MapMode = 5
  Placement = pos=(0,0,-3) rot=(0,0,1;0rad)
  sketch-geometry (7):
    g0: LineSegment StartX=7.62102 StartY=0 StartZ=0 EndX=3.81051 EndY=6.6 EndZ=0
    g1: LineSegment StartX=3.81051 StartY=6.6 StartZ=0 EndX=-3.81051 EndY=6.6 EndZ=0
    g2: LineSegment StartX=-3.81051 StartY=6.6 StartZ=0 EndX=-7.62102 EndY=1.714e-13 EndZ=0
    g3: LineSegment StartX=-7.62102 StartY=1.714e-13 StartZ=0 EndX=-3.81051 EndY=-6.6 EndZ=0
    g4: LineSegment StartX=-3.81051 StartY=-6.6 StartZ=0 EndX=3.81051 EndY=-6.6 EndZ=0
    g5: LineSegment StartX=3.81051 StartY=-6.6 StartZ=0 EndX=7.62102 EndY=0 EndZ=0
    g6: Circle [constr] CenterX=0 CenterY=0 CenterZ=0 NormalX=0 NormalY=0 NormalZ=1 AngleXU=0 Radius=7.62102
  constraints (16):
    c: Coincident(g0,g1)
    c: Coincident(g1,g2)
    c: Coincident(g2,g3)
    c: Coincident(g3,g4)
    c: Coincident(g4,g5)
    c: Coincident(g5,g0)
    c: Equal(g0, g1-g5) x5
    c: PointOnObject(g0,g6)
    c: PointOnObject(g1,g6)
    c: PointOnObject(g2,g6)
    c: PointOnObject(g3,g6)
    c: PointOnObject(g4,g6)
    c: PointOnObject(g5,g6)
    c: Coincident(g6,g-1)
    c: PointOnObject(g5,g-1)
    c: DistanceY(g4,g0) = 13.2
FEATURE [Sketcher::SketchObject] Sketch021
  ArcFitTolerance = 0
  AttachmentSupport = -> [XY_Plane012]
  FullyConstrained = false
  MakeInternals = false
  MapMode = 5
  sketch-geometry (20):
    g0: LineSegment [constr] StartX=0 StartY=12 StartZ=0 EndX=-10.3923 EndY=6 EndZ=0
    g1: LineSegment [constr] StartX=-10.3923 StartY=6 StartZ=0 EndX=-10.3923 EndY=-6 EndZ=0
    g2: LineSegment [constr] StartX=-10.3923 StartY=-6 StartZ=0 EndX=0 EndY=-12 EndZ=0
    g3: LineSegment [constr] StartX=0 StartY=-12 StartZ=0 EndX=10.3923 EndY=-6 EndZ=0
    g4: LineSegment [constr] StartX=10.3923 StartY=-6 StartZ=0 EndX=10.3923 EndY=6 EndZ=0
    g5: LineSegment [constr] StartX=10.3923 StartY=6 StartZ=0 EndX=0 EndY=12 EndZ=0
    g6: Circle [constr] CenterX=0 CenterY=0 CenterZ=0 NormalX=0 NormalY=0 NormalZ=1 AngleXU=0 Radius=12
    g7: ArcOfCircle CenterX=0 CenterY=12 CenterZ=0 NormalX=0 NormalY=0 NormalZ=1 AngleXU=0 Radius=3 StartAngle=3.92621 EndAngle=5.49857
    g8: ArcOfCircle CenterX=-10.3923 CenterY=6 CenterZ=0 NormalX=0 NormalY=0 NormalZ=1 AngleXU=0 Radius=3 StartAngle=4.97341 EndAngle=6.54577
    g9: ArcOfCircle CenterX=-10.3923 CenterY=-6 CenterZ=0 NormalX=0 NormalY=0 NormalZ=1 AngleXU=0 Radius=3 StartAngle=6.0206 EndAngle=7.59297
    g10: ArcOfCircle CenterX=0 CenterY=-12 CenterZ=0 NormalX=0 NormalY=0 NormalZ=1 AngleXU=0 Radius=3 StartAngle=0.784615 EndAngle=2.35698
    g11: ArcOfCircle CenterX=10.3923 CenterY=-6 CenterZ=0 NormalX=0 NormalY=0 NormalZ=1 AngleXU=0 Radius=3 StartAngle=1.83181 EndAngle=3.40418
    g12: ArcOfCircle CenterX=10.3923 CenterY=6 CenterZ=0 NormalX=0 NormalY=0 NormalZ=1 AngleXU=0 Radius=3 StartAngle=2.87901 EndAngle=4.45137
    g13: ArcOfCircle CenterX=4.39482 CenterY=7.61205 CenterZ=0 NormalX=0 NormalY=0 NormalZ=1 AngleXU=0 Radius=3.21036 StartAngle=6.0206 EndAngle=8.64016
    g14: ArcOfCircle CenterX=-4.39482 CenterY=7.61205 CenterZ=0 NormalX=0 NormalY=0 NormalZ=1 AngleXU=0 Radius=3.21036 StartAngle=0.784615 EndAngle=3.40418
    g15: ArcOfCircle CenterX=-8.78964 CenterY=-9e-16 CenterZ=0 NormalX=0 NormalY=0 NormalZ=1 AngleXU=0 Radius=3.21036 StartAngle=1.83181 EndAngle=4.45137
    g16: ArcOfCircle CenterX=-4.39482 CenterY=-7.61205 CenterZ=0 NormalX=0 NormalY=0 NormalZ=1 AngleXU=0 Radius=3.21036 StartAngle=2.87901 EndAngle=5.49857
    g17: ArcOfCircle CenterX=4.39482 CenterY=-7.61205 CenterZ=0 NormalX=0 NormalY=0 NormalZ=1 AngleXU=0 Radius=3.21036 StartAngle=3.92621 EndAngle=6.54577
    g18: ArcOfCircle CenterX=8.78964 CenterY=0 CenterZ=0 NormalX=0 NormalY=0 NormalZ=1 AngleXU=0 Radius=3.21036 StartAngle=4.97341 EndAngle=7.59297
    g19: Circle CenterX=0 CenterY=0 CenterZ=0 NormalX=0 NormalY=0 NormalZ=1 AngleXU=0 Radius=43.58
  constraints (47):
    c: Coincident(g0,g1)
    c: Coincident(g1,g2)
    c: Coincident(g2,g3)
    c: Coincident(g3,g4)
    c: Coincident(g4,g5)
    c: Coincident(g5,g0)
    c: Equal(g0, g1-g5) x5
    c: PointOnObject(g0,g6)
    c: PointOnObject(g1,g6)
    c: PointOnObject(g2,g6)
    c: PointOnObject(g3,g6)
    c: PointOnObject(g5,g6)
    c: Coincident(g6,g-1)
    c: Radius(g6) = 12
    c: Coincident(g7,g0)
    c: Coincident(g8,g0)
    c: Coincident(g9,g1)
    c: Coincident(g10,g2)
    c: Coincident(g11,g3)
    c: Coincident(g12,g4)
    c: Equal(g11,g12)
    c: Equal(g12,g7)
    c: Equal(g7,g8)
    c: Equal(g8,g9)
    c: Equal(g9,g10)
    c: PointOnObject(g18,g-1)
    c: Tangent(g18,g12) = 1.5708
    c: Tangent(g13,g12) = 1.5708
    c: Radius(g12) = 3
    c: Tangent(g13,g7) = 1.5708
    c: Tangent(g14,g7) = 1.5708
    c: Tangent(g14,g8) = 1.5708
    c: Tangent(g15,g8) = 1.5708
    c: Tangent(g15,g9) = 1.5708
    c: Tangent(g16,g9) = 1.5708
    c: Tangent(g16,g10) = 1.5708
    c: Tangent(g17,g10) = 1.5708
    c: Tangent(g17,g11) = 1.5708
    c: Tangent(g18,g11) = 1.5708
    c: PointOnObject(g7,g-2)
    c: Tangent(g18,g6)
    c: Coincident(g19,g6)
    c: Tangent(g17,g6)
    c: Tangent(g13,g6)
    c: Tangent(g14,g6)
    c: Tangent(g15,g6)
    c: Tangent(g16,g6)
FEATURE [PartDesign::Pocket] Pocket004
  BaseFeature = -> Revolution001
  Direction = (0,0,-1)
  Length = 5
  Length2 = 5
  Placement = pos=(0,0,0) rot=(1,0,0;1.5708rad)
  Profile = -> Sketch021
  ReferenceAxis = -> Sketch021 [N_Axis]
  Suppressed = false
  Type = 1
FEATURE [PartDesign::Pocket] Pocket005
  BaseFeature = -> Pocket004
  Direction = (0,0,-1)
  Length = 6.5
  Length2 = 5
  Placement = pos=(0,0,0) rot=(1,0,0;1.5708rad)
  Profile = -> Sketch020
  ReferenceAxis = -> Sketch020 [N_Axis]
  Suppressed = false
  Type = 0
FEATURE [PartDesign::Body] Body012  label="Exterieur Boulon M8 001"
  AllowCompound = false
  Group = -> [Sketch019,Sketch020,Sketch021,Revolution001,Pocket004,Pocket005]
  Origin = -> Origin012
  Placement = pos=(28,-70,0) rot=(-1,0,0;1.5708rad)
  Tip = -> Pocket005
  expr: .Placement.Base.y = -70 - Spreadsheet.eclate * 20
FEATURE [TechDraw::DrawSVGTemplate] Template
  EditableTexts = Designed_by_Name=Alliaume; Drawing_number=A; FC-Date=2024/05/01; FC-SC=1:1; FC-SH=1/1; FC-Title=Attache remorque; Subtitle=Pour L'Incongrue; Weight=TBD
  Height = 210
  Orientation = 1
  Width = 297
FEATURE [TechDraw::DrawViewPart] View  label="Contre plaque"
  CoarseView = false
  Direction = (0,1,0)
  Focus = 100
  HardHidden = false
  IsoCount = 0
  IsoHidden = false
  IsoVisible = false
  LockPosition = false
  Perspective = false
  Rotation = 0
  ScaleType = 0
  ScrubCount = 1
  SeamHidden = false
  SeamVisible = true
  SmoothHidden = false
  SmoothVisible = true
  Source = -> [Body008]
  X = 74.9625
  XDirection = (-1,0,0)
  Y = 33.5708
FEATURE [TechDraw::DrawViewDimension] Dimension
  AngleOverride = false
  Arbitrary = false
  ArbitraryTolerances = false
  EqualTolerance = true
  ExtensionAngle = 0
  FormatSpec = ⌀%.2w
  FormatSpecOverTolerance = %+.2w
  FormatSpecUnderTolerance = %+.2w
  Inverted = false
  LineAngle = 0
  LockPosition = false
  MeasureType = 1
  OverTolerance = 0
  References2D = -> [View]
  Rotation = 0
  ScaleType = 0
  TheoreticalExact = false
  Type = 5
  UnderTolerance = 0
  X = 33.6515
  Y = 11.0536
FEATURE [TechDraw::DrawViewDimension] Dimension001
  AngleOverride = false
  Arbitrary = false
  ArbitraryTolerances = false
  EqualTolerance = true
  ExtensionAngle = 0
  FormatSpec = %.2w
  FormatSpecOverTolerance = %+.2w
  FormatSpecUnderTolerance = %+.2w
  Inverted = false
  LineAngle = 0
  LockPosition = false
  MeasureType = 1
  OverTolerance = 0
  References2D = -> [View]
  Rotation = 0
  ScaleType = 0
  TheoreticalExact = false
  Type = 1
  UnderTolerance = 0
  X = 5.78502
  Y = -5.38639
FEATURE [TechDraw::DrawViewDimension] Dimension002
  AngleOverride = false
  Arbitrary = false
  ArbitraryTolerances = false
  EqualTolerance = true
  ExtensionAngle = 0
  FormatSpec = %.2w
  FormatSpecOverTolerance = %+.2w
  FormatSpecUnderTolerance = %+.2w
  Inverted = false
  LineAngle = 0
  LockPosition = false
  MeasureType = 1
  OverTolerance = 0
  References2D = -> [View]
  Rotation = 0
  ScaleType = 0
  TheoreticalExact = false
  Type = 1
  UnderTolerance = 0
  X = 51.2332
  Y = -8.72734
FEATURE [TechDraw::DrawViewDimension] Dimension003
  AngleOverride = false
  Arbitrary = false
  ArbitraryTolerances = false
  EqualTolerance = true
  ExtensionAngle = 0
  FormatSpec = %.2w
  FormatSpecOverTolerance = %+.2w
  FormatSpecUnderTolerance = %+.2w
  Inverted = false
  LineAngle = 0
  LockPosition = false
  MeasureType = 1
  OverTolerance = 0
  References2D = -> [View]
  Rotation = 0
  ScaleType = 0
  TheoreticalExact = false
  Type = 2
  UnderTolerance = 0
  X = -46.9069
  Y = 2.21453
FEATURE [TechDraw::DrawViewDimension] Dimension004
  AngleOverride = false
  Arbitrary = false
  ArbitraryTolerances = false
  EqualTolerance = true
  ExtensionAngle = 0
  FormatSpec = %.2w
  FormatSpecOverTolerance = %+.2w
  FormatSpecUnderTolerance = %+.2w
  Inverted = false
  LineAngle = 0
  LockPosition = false
  MeasureType = 1
  OverTolerance = 0
  References2D = -> [View]
  Rotation = 0
  ScaleType = 0
  TheoreticalExact = false
  Type = 1
  UnderTolerance = 0
  X = -54.5352
  Y = -12.9609
FEATURE [TechDraw::DrawViewDimension] Dimension005
  AngleOverride = false
  Arbitrary = false
  ArbitraryTolerances = false
  EqualTolerance = true
  ExtensionAngle = 0
  FormatSpec = ⌀%.2w
  FormatSpecOverTolerance = %+.2w
  FormatSpecUnderTolerance = %+.2w
  Inverted = false
  LineAngle = 0
  LockPosition = false
  MeasureType = 1
  OverTolerance = 0
  References2D = -> [View]
  Rotation = 0
  ScaleType = 0
  TheoreticalExact = false
  Type = 5
  UnderTolerance = 0
  X = -18.5642
  Y = 9.44529
FEATURE [Sketcher::SketchObject] Sketch022
  ArcFitTolerance = 0
  AttachmentSupport = -> [XZ_Plane013]
  FullyConstrained = true
  MakeInternals = false
  MapMode = 5
  Placement = pos=(0,0,0) rot=(1,0,0;1.5708rad)
  sketch-geometry (1):
    g0: Circle CenterX=0 CenterY=0 CenterZ=0 NormalX=0 NormalY=0 NormalZ=1 AngleXU=0 Radius=3.3
  constraints (2):
    c: Coincident(g0,g-1)
    c: Radius(g0) = 3.3
FEATURE [PartDesign::Pad] Pad012
  Direction = (0,-1,2e-16)
  Length = 60
  Length2 = 10
  Placement = pos=(0,0,0) rot=(1,0,0;1.5708rad)
  Profile = -> Sketch022
  ReferenceAxis = -> Sketch022 [N_Axis]
  Suppressed = false
  Type = 0
FEATURE [Sketcher::SketchObject] Sketch023
  ArcFitTolerance = 0
  AttachmentSupport = -> [XY_Plane013]
  FullyConstrained = true
  MakeInternals = false
  MapMode = 5
  sketch-geometry (3):
    g0: LineSegment StartX=-3.3 StartY=0 StartZ=0 EndX=-3.3 EndY=-1.25 EndZ=0
    g1: LineSegment StartX=-3.3 StartY=-1.25 StartZ=0 EndX=-4 EndY=-0.625 EndZ=0
    g2: LineSegment StartX=-4 StartY=-0.625 StartZ=0 EndX=-3.3 EndY=0 EndZ=0
  constraints (9):
    c: Coincident(g0,g1)
    c: Coincident(g1,g2)
    c: Coincident(g2,g0)
    c: Vertical(g0)
    c: DistanceY(g0,g0) = 1.25
    c: DistanceX(g0) = -3.3
    c: PointOnObject(g0,g-1)
    c: DistanceX(g1) = -4
    c: Equal(g1,g2)
FEATURE [PartDesign::AdditiveHelix] AdditiveHelix
  Angle = 0
  Axis = (0,1,0)
  Base = (0,0,0)
  BaseFeature = -> Pad012
  Growth = 0
  HasBeenEdited = true
  Height = 58
  LeftHanded = false
  Mode = 0
  Outside = false
  Pitch = 1.251
  Placement = pos=(0,0,0) rot=(1,0,0;1.5708rad)
  Profile = -> Sketch023
  ReferenceAxis = -> Sketch023 [V_Axis]
  Reversed = true
  Suppressed = false
  Tolerance = 0.1
  Turns = 46.3629
FEATURE [Sketcher::SketchObject] Sketch024
  ArcFitTolerance = 0
  AttachmentSupport = -> [XZ_Plane013]
  FullyConstrained = true
  MakeInternals = false
  MapMode = 5
  Placement = pos=(0,0,0) rot=(1,0,0;1.5708rad)
  sketch-geometry (7):
    g0: LineSegment StartX=3.75278 StartY=6.5 StartZ=0 EndX=-3.75278 EndY=6.5 EndZ=0
    g1: LineSegment StartX=-3.75278 StartY=6.5 StartZ=0 EndX=-7.50555 EndY=2.4e-14 EndZ=0
    g2: LineSegment StartX=-7.50555 StartY=2.4e-14 StartZ=0 EndX=-3.75278 EndY=-6.5 EndZ=0
    g3: LineSegment StartX=-3.75278 StartY=-6.5 StartZ=0 EndX=3.75278 EndY=-6.5 EndZ=0
    g4: LineSegment StartX=3.75278 StartY=-6.5 StartZ=0 EndX=7.50555 EndY=1.42e-14 EndZ=0
    g5: LineSegment StartX=7.50555 StartY=1.42e-14 StartZ=0 EndX=3.75278 EndY=6.5 EndZ=0
    g6: Circle [constr] CenterX=0 CenterY=0 CenterZ=0 NormalX=0 NormalY=0 NormalZ=1 AngleXU=0 Radius=7.50555
  constraints (16):
    c: Coincident(g0,g1)
    c: Coincident(g1,g2)
    c: Coincident(g2,g3)
    c: Coincident(g3,g4)
    c: Coincident(g4,g5)
    c: Coincident(g5,g0)
    c: Equal(g0, g1-g5) x5
    c: PointOnObject(g0,g6)
    c: PointOnObject(g1,g6)
    c: PointOnObject(g2,g6)
    c: PointOnObject(g3,g6)
    c: PointOnObject(g4,g6)
    c: PointOnObject(g5,g6)
    c: Coincident(g6,g-1)
    c: Horizontal(g0)
    c: DistanceY(g3,g0) = 13
FEATURE [PartDesign::Pad] Pad013
  BaseFeature = -> AdditiveHelix
  Direction = (0,-1,2e-16)
  Length = 5.3
  Length2 = 10
  Placement = pos=(0,0,0) rot=(1,0,0;1.5708rad)
  Profile = -> Sketch024
  ReferenceAxis = -> Sketch024 [N_Axis]
  Reversed = true
  Suppressed = false
  Type = 0
FEATURE [PartDesign::Body] Body013  label="Vis M8 60 001"
  AllowCompound = false
  Group = -> [Sketch022,Pad012,Sketch023,AdditiveHelix,Sketch024,Pad013]
  Origin = -> Origin013
  Placement = pos=(-28,-27,0) rot=(0,0,1;0rad)
  Tip = -> Pad013
  expr: .Placement.Base.y = -27 + Spreadsheet.eclate * 50
FEATURE [Part::FeaturePython] Clone007  label="Vis M8 60 002"  # Draft clone (typed FeaturePython)
  AttacherType = Attacher::AttachEngine3D
  Fuse = false
  Objects = -> [Body013]
  Placement = pos=(28,-27,0) rot=(0,0,1;0rad)
  Scale = (1,1,1)
  expr: .Placement.Base.y = -27 + Spreadsheet.eclate * 50
FEATURE [Sketcher::SketchObject] Sketch025
  ArcFitTolerance = 0
  AttachmentSupport = -> [XZ_Plane006]
  FullyConstrained = true
  MakeInternals = false
  MapMode = 5
  Placement = pos=(0,0,0) rot=(1,0,0;1.5708rad)
  sketch-geometry (6):
    g0: LineSegment StartX=-40 StartY=15 StartZ=0 EndX=40 EndY=15 EndZ=0
    g1: LineSegment StartX=40 StartY=15 StartZ=0 EndX=40 EndY=-15 EndZ=0
    g2: LineSegment StartX=40 StartY=-15 StartZ=0 EndX=-40 EndY=-15 EndZ=0
    g3: LineSegment StartX=-40 StartY=-15 StartZ=0 EndX=-40 EndY=15 EndZ=0
    g4: Circle CenterX=-28 CenterY=0 CenterZ=0 NormalX=0 NormalY=0 NormalZ=1 AngleXU=0 Radius=4
    g5: Circle CenterX=28 CenterY=0 CenterZ=0 NormalX=0 NormalY=0 NormalZ=1 AngleXU=0 Radius=4
  constraints (15):
    c: Coincident(g0,g1)
    c: Coincident(g1,g2)
    c: Coincident(g2,g3)
    c: Coincident(g3,g0)
    c: Horizontal(g2)
    c: Vertical(g3)
    c: Symmetric(g1,g0,g-1)
    c: Symmetric(g0,g0,g-2)
    c: Symmetric(g5,g4,g-2)
    c: Equal(g4,g5)
    c: Radius(g5) = 4
    c: DistanceX(g4,g5) = 56
    c: PointOnObject(g5,g-1)
    c: DistanceX(g0,g0) = 80
    c: DistanceY(g1,g1) = 30
FEATURE [PartDesign::Pad] Pad014
  Direction = (0,-1,2e-16)
  Length = 3
  Length2 = 10
  Placement = pos=(0,0,0) rot=(1,0,0;1.5708rad)
  Profile = -> Sketch025
  ReferenceAxis = -> Sketch025 [N_Axis]
  Reversed = true
  Suppressed = false
  Type = 0
FEATURE [PartDesign::Body] Body006  label="Fer Plat 30x3 001"
  AllowCompound = false
  Group = -> [Sketch025,Pad014]
  Origin = -> Origin006
  Placement = pos=(0,-30,0) rot=(0,1,0;3.14159rad)
  Tip = -> Pad014
  expr: .Placement.Base.y = -30 + Spreadsheet.eclate * 40
FEATURE [TechDraw::DrawViewPart] View001  label="Plaque Boulon"
  CoarseView = false
  Direction = (0,1,0)
  Focus = 100
  HardHidden = false
  IsoCount = 0
  IsoHidden = false
  IsoVisible = false
  LockPosition = false
  Perspective = false
  Rotation = 0
  ScaleType = 0
  ScrubCount = 1
  SeamHidden = false
  SeamVisible = true
  SmoothHidden = false
  SmoothVisible = true
  Source = -> [Body006]
  X = 237.526
  XDirection = (1,0,0)
  Y = 166.646
FEATURE [Sketcher::SketchObject] Sketch026
  ArcFitTolerance = 0
  AttachmentSupport = -> [XZ_Plane014]
  FullyConstrained = true
  MakeInternals = false
  MapMode = 5
  Placement = pos=(0,0,0) rot=(1,0,0;1.5708rad)
  sketch-geometry (2):
    g0: Circle CenterX=0 CenterY=0 CenterZ=0 NormalX=0 NormalY=0 NormalZ=1 AngleXU=0 Radius=9
    g1: Circle CenterX=0 CenterY=0 CenterZ=0 NormalX=0 NormalY=0 NormalZ=1 AngleXU=0 Radius=4.2
  constraints (4):
    c: Coincident(g0,g-1)
    c: Coincident(g1,g0)
    c: Radius(g1) = 4.2
    c: Radius(g0) = 9
FEATURE [PartDesign::Pad] Pad015
  Direction = (0,-1,2e-16)
  Length = 1.5
  Length2 = 10
  Placement = pos=(0,0,0) rot=(1,0,0;1.5708rad)
  Profile = -> Sketch026
  ReferenceAxis = -> Sketch026 [N_Axis]
  Suppressed = false
  Type = 0
FEATURE [PartDesign::Body] Body014  label="Rondelle M8 001"
  AllowCompound = false
  Group = -> [Sketch026,Pad015]
  Origin = -> Origin014
  Placement = pos=(28,-45,0) rot=(0,0,1;0rad)
  Tip = -> Pad015
  expr: .Placement.Base.y = -45 + Spreadsheet.eclate * 10
FEATURE [Part::FeaturePython] Clone008  label="Rondelle M8 002"  # Draft clone (typed FeaturePython)
  AttacherType = Attacher::AttachEngine3D
  Fuse = false
  Objects = -> [Body014]
  Placement = pos=(-28,-45,0) rot=(0,0,1;0rad)
  Scale = (1,1,1)
  expr: .Placement.Base.y = -45 + Spreadsheet.eclate * 10
FEATURE [Sketcher::SketchObject] Sketch027
  ArcFitTolerance = 0
  AttachmentSupport = -> [XY_Plane015]
  FullyConstrained = true
  MakeInternals = false
  MapMode = 5
  sketch-geometry (8):
    g0: LineSegment StartX=6.5 StartY=3.75278 StartZ=0 EndX=4e-14 EndY=7.50555 EndZ=0
    g1: LineSegment StartX=4e-14 StartY=7.50555 StartZ=0 EndX=-6.5 EndY=3.75278 EndZ=0
    g2: LineSegment StartX=-6.5 StartY=3.75278 StartZ=0 EndX=-6.5 EndY=-3.75278 EndZ=0
    g3: LineSegment StartX=-6.5 StartY=-3.75278 StartZ=0 EndX=3.91e-14 EndY=-7.50555 EndZ=0
    g4: LineSegment StartX=3.91e-14 StartY=-7.50555 StartZ=0 EndX=6.5 EndY=-3.75278 EndZ=0
    g5: LineSegment StartX=6.5 StartY=-3.75278 StartZ=0 EndX=6.5 EndY=3.75278 EndZ=0
    g6: Circle [constr] CenterX=0 CenterY=0 CenterZ=0 NormalX=0 NormalY=0 NormalZ=1 AngleXU=0 Radius=7.50555
    g7: Circle CenterX=0 CenterY=0 CenterZ=0 NormalX=0 NormalY=0 NormalZ=1 AngleXU=0 Radius=4
  constraints (18):
    c: Coincident(g0,g1)
    c: Coincident(g1,g2)
    c: Coincident(g2,g3)
    c: Coincident(g3,g4)
    c: Coincident(g4,g5)
    c: Coincident(g5,g0)
    c: Equal(g0, g1-g5) x5
    c: PointOnObject(g0,g6)
    c: PointOnObject(g1,g6)
    c: PointOnObject(g2,g6)
    c: PointOnObject(g3,g6)
    c: PointOnObject(g4,g6)
    c: PointOnObject(g5,g6)
    c: Coincident(g6,g-1)
    c: Vertical(g5)
    c: DistanceX(g2,g4) = 13
    c: Coincident(g7,g6)
    c: Radius(g7) = 4
FEATURE [PartDesign::Pad] Pad016
  Direction = (0,0,1)
  Length = 7
  Length2 = 10
  Profile = -> Sketch027
  ReferenceAxis = -> Sketch027 [N_Axis]
  Suppressed = false
  Type = 0
FEATURE [PartDesign::Body] Body015  label="Ecrou M8 001"
  AllowCompound = false
  Group = -> [Sketch027,Pad016]
  Origin = -> Origin015
  Placement = pos=(28,-52,0) rot=(-1,0,0;1.5708rad)
  Tip = -> Pad016
FEATURE [Part::FeaturePython] Clone009  label="Ecrou M8 002"  # Draft clone (typed FeaturePython)
  AttacherType = Attacher::AttachEngine3D
  Fuse = false
  Objects = -> [Body015]
  Placement = pos=(-28,-52,0) rot=(-1,0,0;1.5708rad)
  Scale = (1,1,1)
FEATURE [Part::FeaturePython] Clone010  label="Exterieur Boulon M8 002"  # Draft clone (typed FeaturePython)
  AttacherType = Attacher::AttachEngine3D
  Fuse = false
  Objects = -> [Body012]
  Placement = pos=(-28,-70,0) rot=(-1,0,0;1.5708rad)
  Scale = (1,1,1)
  expr: .Placement.Base.y = -70 - Spreadsheet.eclate * 20
FEATURE [TechDraw::DrawViewDimension] Dimension011
  AngleOverride = false
  Arbitrary = false
  ArbitraryTolerances = false
  EqualTolerance = true
  ExtensionAngle = 0
  FormatSpec = %.2w
  FormatSpecOverTolerance = %+.2w
  FormatSpecUnderTolerance = %+.2w
  Inverted = false
  LineAngle = 0
  LockPosition = false
  MeasureType = 1
  OverTolerance = 0
  References2D = -> [View001]
  Rotation = 0
  ScaleType = 0
  TheoreticalExact = false
  Type = 1
  UnderTolerance = 0
  X = -54.1793
  Y = 22.1168
FEATURE [TechDraw::DrawViewDimension] Dimension012
  AngleOverride = false
  Arbitrary = false
  ArbitraryTolerances = false
  EqualTolerance = true
  ExtensionAngle = 0
  FormatSpec = %.2w
  FormatSpecOverTolerance = %+.2w
  FormatSpecUnderTolerance = %+.2w
  Inverted = false
  LineAngle = 0
  LockPosition = false
  MeasureType = 1
  OverTolerance = 0
  References2D = -> [View001]
  Rotation = 0
  ScaleType = 0
  TheoreticalExact = false
  Type = 1
  UnderTolerance = 0
  X = 0
  Y = 29.6001
FEATURE [TechDraw::DrawViewDimension] Dimension013
  AngleOverride = false
  Arbitrary = false
  ArbitraryTolerances = false
  EqualTolerance = true
  ExtensionAngle = 0
  FormatSpec = ⌀%.2w
  FormatSpecOverTolerance = %+.2w
  FormatSpecUnderTolerance = %+.2w
  Inverted = false
  LineAngle = 0
  LockPosition = false
  MeasureType = 1
  OverTolerance = 0
  References2D = -> [View001]
  Rotation = 0
  ScaleType = 0
  TheoreticalExact = false
  Type = 5
  UnderTolerance = 0
  X = 0
  Y = 0
FEATURE [TechDraw::DrawViewDimension] Dimension014
  AngleOverride = false
  Arbitrary = false
  ArbitraryTolerances = false
  EqualTolerance = true
  ExtensionAngle = 0
  FormatSpec = %.2w
  FormatSpecOverTolerance = %+.2w
  FormatSpecUnderTolerance = %+.2w
  Inverted = false
  LineAngle = 0
  LockPosition = false
  MeasureType = 1
  OverTolerance = 0
  References2D = -> [View001]
  Rotation = 0
  ScaleType = 0
  TheoreticalExact = false
  Type = 1
  UnderTolerance = 0
  X = 0.129672
  Y = 23.8071
FEATURE [TechDraw::DrawViewDimension] Dimension015
  AngleOverride = false
  Arbitrary = false
  ArbitraryTolerances = false
  EqualTolerance = true
  ExtensionAngle = 0
  FormatSpec = %.2w
  FormatSpecOverTolerance = %+.2w
  FormatSpecUnderTolerance = %+.2w
  Inverted = false
  LineAngle = 0
  LockPosition = false
  MeasureType = 1
  OverTolerance = 0
  References2D = -> [View001]
  Rotation = 0
  ScaleType = 0
  TheoreticalExact = false
  Type = 2
  UnderTolerance = 0
  X = -46.6521
  Y = 6.53585
FEATURE [Sketcher::SketchObject] Sketch028
  ArcFitTolerance = 0
  AttachmentSupport = -> [XZ_Plane003]
  FullyConstrained = true
  MakeInternals = false
  MapMode = 5
  Placement = pos=(0,0,0) rot=(1,0,0;1.5708rad)
  sketch-geometry (1):
    g0: Circle CenterX=0 CenterY=0 CenterZ=0 NormalX=0 NormalY=0 NormalZ=1 AngleXU=0 Radius=6
  constraints (2):
    c: Coincident(g0,g-1)
    c: Radius(g0) = 6
FEATURE [PartDesign::Pocket] Pocket
  BaseFeature = -> Pad003
  Direction = (0,1,-2e-16)
  Length = 5
  Length2 = 5
  Placement = pos=(0,0,0) rot=(0.57735,0.57735,0.57735;2.0944rad)
  Profile = -> Sketch028
  ReferenceAxis = -> Sketch028 [N_Axis]
  Suppressed = false
  Type = 0
FEATURE [PartDesign::Body] Body003  label="Fer Plat Remorque 30x30x3 "
  AllowCompound = false
  Group = -> [Sketch003,Pad003,Sketch028,Pocket]
  Origin = -> Origin003
  Placement = pos=(0,9,0) rot=(0,1,0;1.5708rad)
  Tip = -> Pocket
  expr: .Placement.Base.y = 9 + Spreadsheet.eclate * 90
FEATURE [TechDraw::DrawViewPart] View002  label="Plaque tige"
  CoarseView = false
  Direction = (0,1,0)
  Focus = 100
  HardHidden = false
  IsoCount = 0
  IsoHidden = false
  IsoVisible = false
  LockPosition = false
  Perspective = false
  Rotation = 0
  ScaleType = 0
  ScrubCount = 1
  SeamHidden = false
  SeamVisible = true
  SmoothHidden = false
  SmoothVisible = true
  Source = -> [Body003]
  X = 259.605
  XDirection = (-1,0,0)
  Y = 114.971
FEATURE [TechDraw::DrawViewDimension] Dimension016
  AngleOverride = false
  Arbitrary = false
  ArbitraryTolerances = false
  EqualTolerance = true
  ExtensionAngle = 0
  FormatSpec = ⌀%.2w
  FormatSpecOverTolerance = %+.2w
  FormatSpecUnderTolerance = %+.2w
  Inverted = false
  LineAngle = 0
  LockPosition = false
  MeasureType = 1
  OverTolerance = 0
  References2D = -> [View002]
  Rotation = 0
  ScaleType = 0
  TheoreticalExact = false
  Type = 5
  UnderTolerance = 0
  X = 7.35949
  Y = 10.4457
FEATURE [TechDraw::DrawViewDimension] Dimension017
  AngleOverride = false
  Arbitrary = false
  ArbitraryTolerances = false
  EqualTolerance = true
  ExtensionAngle = 0
  FormatSpec = %.2w
  FormatSpecOverTolerance = %+.2w
  FormatSpecUnderTolerance = %+.2w
  Inverted = false
  LineAngle = 0
  LockPosition = false
  MeasureType = 1
  OverTolerance = 0
  References2D = -> [View002]
  Rotation = 0
  ScaleType = 0
  TheoreticalExact = false
  Type = 1
  UnderTolerance = 0
  X = 2.13663
  Y = 26.5213
FEATURE [TechDraw::DrawViewDimension] Dimension018
  AngleOverride = false
  Arbitrary = false
  ArbitraryTolerances = false
  EqualTolerance = true
  ExtensionAngle = 0
  FormatSpec = %.2w
  FormatSpecOverTolerance = %+.2w
  FormatSpecUnderTolerance = %+.2w
  Inverted = false
  LineAngle = 0
  LockPosition = false
  MeasureType = 1
  OverTolerance = 0
  References2D = -> [View002]
  Rotation = 0
  ScaleType = 0
  TheoreticalExact = false
  Type = 2
  UnderTolerance = 0
  X = 19.8982
  Y = 3.92442
FEATURE [Spreadsheet::Sheet] Spreadsheet
  cells = A3='Vue eclaté ?; B3(eclate)=0; C3='1 ou 0
FEATURE [Part::FeaturePython] Clone011  label="Ecrou M8 003"  # Draft clone (typed FeaturePython)
  AttacherType = Attacher::AttachEngine3D
  Fuse = false
  Objects = -> [Body015]
  Placement = pos=(28,-37,0) rot=(-1,0,0;1.5708rad)
  Scale = (1,1,1)
  expr: .Placement.Base.y = -37 + Spreadsheet.eclate * 30
FEATURE [Part::FeaturePython] Clone012  label="Ecrou M8 004"  # Draft clone (typed FeaturePython)
  AttacherType = Attacher::AttachEngine3D
  Fuse = false
  Objects = -> [Clone011]
  Placement = pos=(-27.5,-37,-3.3e-15) rot=(-1,0,0;1.5708rad)
  Scale = (1,1,1)
  expr: .Placement.Base.y = -37 + Spreadsheet.eclate * 30
FEATURE [TechDraw::DrawViewPart] View003  label="Vue éclatée"
  CoarseView = false
  Direction = (0.652,0.628,0.424)
  Focus = 100
  HardHidden = false
  IsoCount = 0
  IsoHidden = false
  IsoVisible = false
  LockPosition = false
  Perspective = false
  Rotation = 0
  ScaleType = 0
  ScrubCount = 1
  SeamHidden = false
  SeamVisible = true
  SmoothHidden = false
  SmoothVisible = true
  Source = -> [Body,Body001,Clone,Body002,Clone001,Clone002,Body003,Clone003,Body004,Body005,Clone004,Body006,Body007,Body008,Body012,Body013,Clone007,Body014,Clone008,Body015,Clone009,Clone010,Clone011,Clone012]
  X = 137.817
  XDirection = (-0.703,0.711,0.027)
  Y = 128.028
FEATURE [TechDraw::DrawViewBalloon] Balloon
  BubbleShape = 6
  EndType = 0
  EndTypeScale = 1
  KinkLength = 5
  LockPosition = false
  OriginX = -23.3218
  OriginY = 32.7626
  Rotation = 0
  ScaleType = 0
  ShapeScale = 1
  SourceView = -> View003
  Text = Ecrou M8
  TextWrapLen = -1
  X = -16.1416
  Y = 52.2878
FEATURE [TechDraw::DrawViewBalloon] Balloon002
  BubbleShape = 6
  EndType = 0
  EndTypeScale = 1
  KinkLength = 5
  LockPosition = false
  OriginX = 37.3598
  OriginY = 5.92431
  Rotation = 0
  ScaleType = 0
  ShapeScale = 1
  SourceView = -> View003
  Text = Ecrou M10 Percé
  TextWrapLen = -1
  X = 71.6039
  Y = 11.2053
FEATURE [TechDraw::DrawViewBalloon] Balloon003
  BubbleShape = 6
  EndType = 0
  EndTypeScale = 1
  KinkLength = 5
  LockPosition = false
  OriginX = -1.95556
  OriginY = -24.2141
  Rotation = 0
  ScaleType = 0
  ShapeScale = 1
  SourceView = -> View003
  Text = Ecrou M10
  TextWrapLen = -1
  X = -29.4362
  Y = -32.2277
FEATURE [TechDraw::DrawViewBalloon] Balloon004
  BubbleShape = 6
  EndType = 0
  EndTypeScale = 1
  KinkLength = 5
  LockPosition = false
  OriginX = 38.8376
  OriginY = -44.1892
  Rotation = 0
  ScaleType = 0
  ShapeScale = 1
  SourceView = -> View003
  Text = Ecrou M10
  TextWrapLen = -1
  X = 16.8173
  Y = -50.3036
FEATURE [TechDraw::DrawViewBalloon] Balloon005
  BubbleShape = 6
  EndType = 0
  EndTypeScale = 1
  KinkLength = 5
  LockPosition = false
  OriginX = 53.6917
  OriginY = 2.30976
  Rotation = 0
  ScaleType = 0
  ShapeScale = 1
  SourceView = -> View003
  Text = Ecrou M10 Percé
  TextWrapLen = -1
  X = 82.4756
  Y = 2.13051
FEATURE [TechDraw::DrawViewBalloon] Balloon006
  BubbleShape = 6
  EndType = 0
  EndTypeScale = 1
  KinkLength = 5
  LockPosition = false
  OriginX = 75.9625
  OriginY = -26.4994
  Rotation = 0
  ScaleType = 0
  ShapeScale = 1
  SourceView = -> View003
  Text = Ecrou M10
  TextWrapLen = -1
  X = 93.1136
  Y = -20.7436
FEATURE [TechDraw::DrawViewBalloon] Balloon007
  BubbleShape = 6
  EndType = 0
  EndTypeScale = 1
  KinkLength = 5
  LockPosition = false
  OriginX = 26.285
  OriginY = -20.8473
  Rotation = 0
  ScaleType = 0
  ShapeScale = 1
  SourceView = -> View003
  Text = Ecrou M10
  TextWrapLen = -1
  X = 7.11347
  Y = -31.7097
FEATURE [TechDraw::DrawViewBalloon] Balloon008
  BubbleShape = 6
  EndType = 0
  EndTypeScale = 1
  KinkLength = 5
  LockPosition = false
  OriginX = 43.8208
  OriginY = -24.0425
  Rotation = 0
  ScaleType = 0
  ShapeScale = 1
  SourceView = -> View003
  Text = Tige Filetée M10 30mm
  TextWrapLen = -1
  X = 5.4197
  Y = -40.8399
FEATURE [TechDraw::DrawViewBalloon] Balloon009
  BubbleShape = 6
  EndType = 0
  EndTypeScale = 1
  KinkLength = 5
  LockPosition = false
  OriginX = -67.1115
  OriginY = 11.0567
  Rotation = 0
  ScaleType = 0
  ShapeScale = 1
  SourceView = -> View003
  Text = Ecrou M8
  TextWrapLen = -1
  X = -94.1173
  Y = -8.35217
FEATURE [TechDraw::DrawViewBalloon] Balloon010
  BubbleShape = 6
  EndType = 0
  EndTypeScale = 1
  KinkLength = 5
  LockPosition = false
  OriginX = -35.1125
  OriginY = -3.15067
  Rotation = 0
  ScaleType = 0
  ShapeScale = 1
  SourceView = -> View003
  Text = Ecrou M8
  TextWrapLen = -1
  X = -59.7443
  Y = -23.5092
FEATURE [TechDraw::DrawViewBalloon] Balloon011
  BubbleShape = 6
  EndType = 0
  EndTypeScale = 1
  KinkLength = 5
  LockPosition = false
  OriginX = 16.7993
  OriginY = -14.9554
  Rotation = 0
  ScaleType = 0
  ShapeScale = 1
  SourceView = -> View003
  Text = Tige Filetée M10 36mm
  TextWrapLen = -1
  X = -38.6949
  Y = -39.5872
FEATURE [TechDraw::DrawViewBalloon] Balloon012
  BubbleShape = 6
  EndType = 0
  EndTypeScale = 1
  KinkLength = 5
  LockPosition = false
  OriginX = 90.1033
  OriginY = -47.0799
  Rotation = 0
  ScaleType = 0
  ShapeScale = 1
  SourceView = -> View003
  Text = Tige filetée de la remorque
  TextWrapLen = -1
  X = 48.8533
  Y = -61.7407
FEATURE [TechDraw::DrawViewBalloon] Balloon013
  BubbleShape = 6
  EndType = 0
  EndTypeScale = 1
  KinkLength = 5
  LockPosition = false
  OriginX = -61.3488
  OriginY = 0.534761
  Rotation = 0
  ScaleType = 0
  ShapeScale = 1
  SourceView = -> View003
  Text = Rondelle M8
  TextWrapLen = -1
  X = -91.9156
  Y = -18.6367
FEATURE [TechDraw::DrawViewBalloon] Balloon014
  BubbleShape = 6
  EndType = 0
  EndTypeScale = 1
  KinkLength = 5
  LockPosition = false
  OriginX = -19.9204
  OriginY = 27.0904
  Rotation = 0
  ScaleType = 0
  ShapeScale = 1
  SourceView = -> View003
  Text = Rondelle M8
  TextWrapLen = -1
  X = -9.17908
  Y = 45.1912
FEATURE [TechDraw::DrawViewBalloon] Balloon015
  BubbleShape = 6
  EndType = 0
  EndTypeScale = 1
  KinkLength = 5
  LockPosition = false
  OriginX = -42.6989
  OriginY = 50.6714
  Rotation = 0
  ScaleType = 0
  ShapeScale = 1
  SourceView = -> View003
  Text = Tige de selle
  TextWrapLen = -1
  X = -13.915
  Y = 59.276
FEATURE [TechDraw::DrawViewBalloon] Balloon016
  BubbleShape = 6
  EndType = 0
  EndTypeScale = 1
  KinkLength = 5
  LockPosition = false
  OriginX = 29.7493
  OriginY = 10.0899
  Rotation = 0
  ScaleType = 0
  ShapeScale = 1
  SourceView = -> View003
  Text = Vis M8x60
  TextWrapLen = -1
  X = 46.4256
  Y = 16.3205
FEATURE [TechDraw::DrawViewBalloon] Balloon017
  BubbleShape = 6
  EndType = 0
  EndTypeScale = 1
  KinkLength = 5
  LockPosition = false
  OriginX = -14.5671
  OriginY = -18.1765
  Rotation = 0
  ScaleType = 0
  ShapeScale = 1
  SourceView = -> View003
  Text = Vis M8x60
  TextWrapLen = -1
  X = -59.3781
  Y = -31.4129
FEATURE [TechDraw::DrawViewBalloon] Balloon018
  BubbleShape = 6
  EndType = 0
  EndTypeScale = 1
  KinkLength = 5
  LockPosition = false
  OriginX = 5.80404
  OriginY = 19.3246
  Rotation = 0
  ScaleType = 0
  ShapeScale = 1
  SourceView = -> View003
  Text = Ecrou M8
  TextWrapLen = -1
  X = 29.3651
  Y = 39.562
FEATURE [TechDraw::DrawViewBalloon] Balloon019
  BubbleShape = 6
  EndType = 0
  EndTypeScale = 1
  KinkLength = 5
  LockPosition = false
  OriginX = -75.0766
  OriginY = 37.5086
  Rotation = 0
  ScaleType = 0
  ShapeScale = 1
  SourceView = -> View003
  Text = Contre plaque (voir détail)
  TextWrapLen = -1
  X = -96.8595
  Y = 45.1636
FEATURE [TechDraw::DrawViewBalloon] Balloon020
  BubbleShape = 6
  EndType = 0
  EndTypeScale = 1
  KinkLength = 5
  LockPosition = false
  OriginX = -1.32392
  OriginY = 12.7426
  Rotation = 0
  ScaleType = 0
  ShapeScale = 1
  SourceView = -> View003
  Text = Plaque Boulon (voir détail)
  TextWrapLen = -1
  X = 34.3447
  Y = 30.606
FEATURE [TechDraw::DrawViewBalloon] Balloon021
  BubbleShape = 6
  EndType = 0
  EndTypeScale = 1
  KinkLength = 5
  LockPosition = false
  OriginX = 65.9417
  OriginY = -13.7684
  Rotation = 0
  ScaleType = 0
  ShapeScale = 1
  SourceView = -> View003
  Text = Plaque tige
  TextWrapLen = -1
  X = 92.589
  Y = -7.77519
FEATURE [TechDraw::DrawViewBalloon] Balloon022
  BubbleShape = 6
  EndType = 0
  EndTypeScale = 1
  KinkLength = 5
  LockPosition = false
  OriginX = -106.432
  OriginY = 16.233
  Rotation = 0
  ScaleType = 0
  ShapeScale = 1
  SourceView = -> View003
  Text = Bouton rotatif (Plastique + Ecrou M8)
  TextWrapLen = -1
  X = -92.1293
  Y = 64.9587
FEATURE [TechDraw::DrawViewBalloon] Balloon023
  BubbleShape = 6
  EndType = 0
  EndTypeScale = 1
  KinkLength = 5
  LockPosition = false
  OriginX = -67.0555
  OriginY = 49.2932
  Rotation = 0
  ScaleType = 0
  ShapeScale = 1
  SourceView = -> View003
  Text = Bouton rotatif (Plastique + Ecrou M8)
  TextWrapLen = -1
  X = -90.5003
  Y = 57.1857
FEATURE [TechDraw::DrawViewAnnotation] Annotation
  Font = Open Sans
  LineSpace = 80
  LockPosition = false
  MaxWidth = -1
  Rotation = 0
  ScaleType = 0
  Text = Non représenté : | - 2 manchons de 30mm de chambre à air | * Un sur contreplaque | *  L'autre sur la calle tige de selle | - Fin de vis M8 : méplat + percage 3mm | * Insertion d'un bout de fil de fer pour éviter de perdre les boutons
  TextSize = 3
  TextStyle = 0
  X = 64.9342
  Y = 71.0514
FEATURE [TechDraw::DrawViewBalloon] Balloon024
  BubbleShape = 6
  EndType = 0
  EndTypeScale = 1
  KinkLength = 5
  LockPosition = false
  OriginX = 5.091
  OriginY = 33.754
  Rotation = 0
  ScaleType = 0
  ShapeScale = 1
  SourceView = -> View003
  Text = Calle tige de selle (Plastique ou bois)
  TextWrapLen = -1
  X = 30.5513
  Y = 65.6241
FEATURE [TechDraw::DrawPage] Page
  KeepUpdated = true
  NextBalloonIndex = 30
  ProjectionType = 0
  Template = -> Template
  Views = -> [View,Dimension,Dimension001,Dimension002,Dimension003,Dimension004,Dimension005,View001,Dimension011,Dimension012,Dimension013,Dimension014,Dimension015,View002,Dimension016,Dimension017,Dimension018,View003,Balloon,Balloon002,Balloon003,Balloon004,Balloon005,Balloon006,Balloon007,Balloon008,Balloon009,Balloon010,Balloon011,Balloon012,Balloon013,Balloon014,Balloon015,Balloon016,Balloon017,+8 more]
